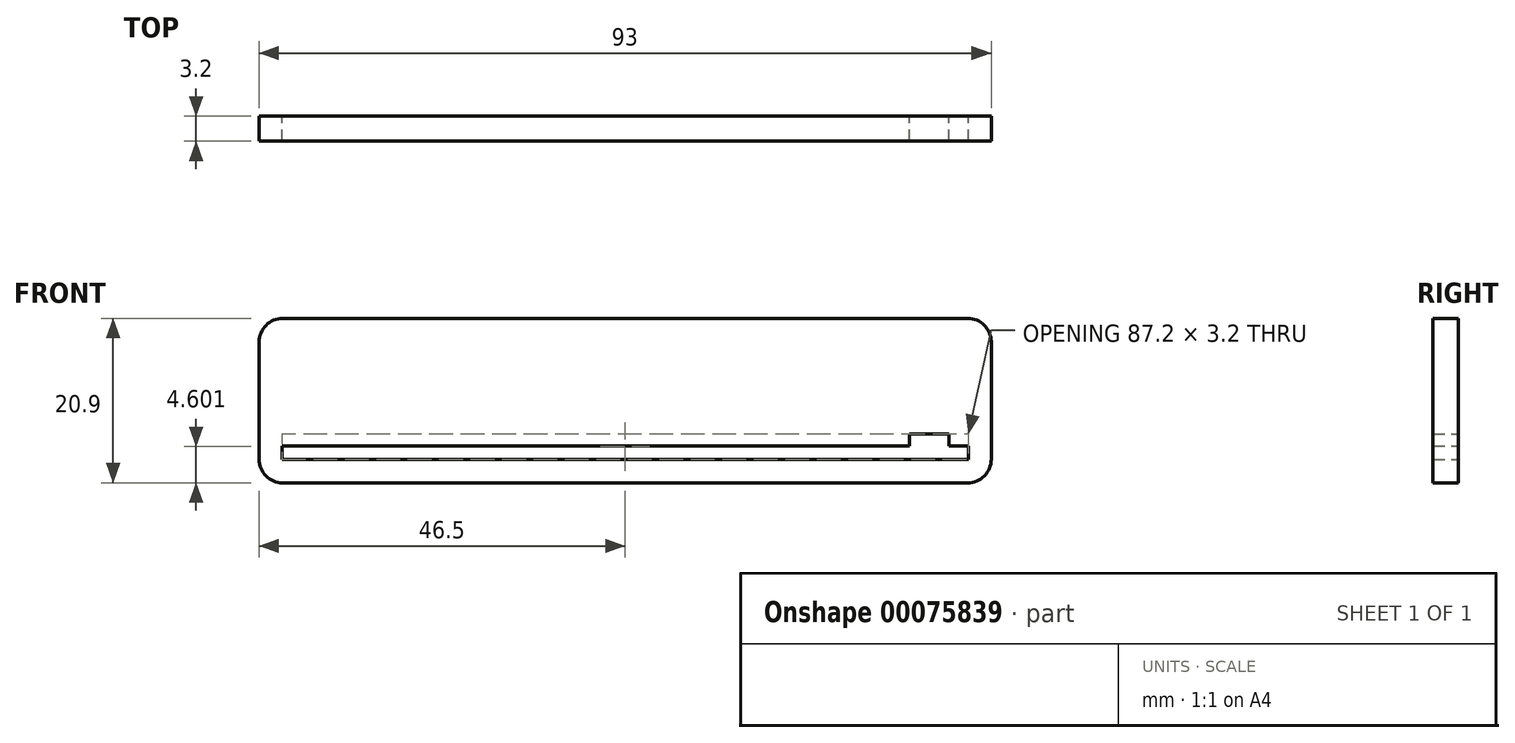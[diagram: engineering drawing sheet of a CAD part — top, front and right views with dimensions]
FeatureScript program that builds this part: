
annotation { "Feature Type Name" : "Feature", "Feature Type Description" : "" }
export const myFeature = defineFeature(function(context is Context, id is Id, definition is map)
    precondition{}
    {
        {
            var Q0;
            Q0=qCreatedBy(makeId("Front.planeOp"),FACE);
            var sketch = newSketch(context, id + "F0", { "sketchPlane" : qUnion([Q0])});
            skLineSegment(sketch, "E0", {"start": v(-56.25, -14.43) * mm, "end": v(-56.25, -16.13) * mm});
            skLineSegment(sketch, "E1", {"start": v(-56.25, -16.13) * mm, "end": v(30.95, -16.13) * mm});
            skLineSegment(sketch, "E2", {"start": v(30.95, -16.13) * mm, "end": v(30.95, -14.43) * mm});
            skLineSegment(sketch, "E3.bottom", {"start": v(-56.15, 1.77) * mm, "end": v(30.85, 1.77) * mm});
            skLineSegment(sketch, "E3.top", {"start": v(-56.15, -19.13) * mm, "end": v(30.85, -19.13) * mm});
            skLineSegment(sketch, "E3.left", {"start": v(-59.15, -1.23) * mm, "end": v(-59.15, -16.13) * mm});
            skLineSegment(sketch, "E3.right", {"start": v(33.85, -1.23) * mm, "end": v(33.85, -16.13) * mm});
            skPoint(sketch, "E4.visualSharp", {"position": v(-59.15, 1.77) * mm});
            skArc(sketch, "E4.filletArc", {"start": v(-56.15, 1.77) * mm, "mid": v(-58.27, 0.9) * mm, "end": v(-59.15, -1.23) * mm});
            skPoint(sketch, "E5.visualSharp", {"position": v(33.85, 1.77) * mm});
            skArc(sketch, "E5.filletArc", {"start": v(33.85, -1.23) * mm, "mid": v(32.97, 0.9) * mm, "end": v(30.85, 1.77) * mm});
            skPoint(sketch, "E6.visualSharp", {"position": v(33.85, -19.13) * mm});
            skArc(sketch, "E6.filletArc", {"start": v(30.85, -19.13) * mm, "mid": v(32.97, -18.25) * mm, "end": v(33.85, -16.13) * mm});
            skPoint(sketch, "E7.visualSharp", {"position": v(-59.15, -19.13) * mm});
            skArc(sketch, "E7.filletArc", {"start": v(-59.15, -16.13) * mm, "mid": v(-58.27, -18.25) * mm, "end": v(-56.15, -19.13) * mm});
            skLineSegment(sketch, "E8", {"start": v(30.95, -14.43) * mm, "end": v(28.45, -14.43) * mm});
            skLineSegment(sketch, "E9", {"start": v(28.45, -14.43) * mm, "end": v(28.45, -12.93) * mm});
            skLineSegment(sketch, "E10", {"start": v(28.45, -12.93) * mm, "end": v(23.45, -12.93) * mm});
            skLineSegment(sketch, "E11", {"start": v(23.45, -12.93) * mm, "end": v(23.45, -14.43) * mm});
            skLineSegment(sketch, "E12", {"start": v(23.45, -14.43) * mm, "end": v(-56.25, -14.43) * mm});
            skSolve(sketch);
        }
        {
            var Q0;
            Q0 = qSketchRegion(id + "F0", true);
            extrude(context, id + "F1", {"entities" : qUnion([Q0]), "depth" : 3.2 * mm});
        }
    });
